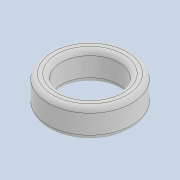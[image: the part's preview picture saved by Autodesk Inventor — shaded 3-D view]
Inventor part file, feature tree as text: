
AUTODESK INVENTOR PART (.ipt)
format: ipt  version: 2020 (Build 240168000, 168)  size: 139,264 bytes
history: native  units: mm
features: extrude x1, fillet x1, sketch x1
ambient origin geometry x8: Origin, YZ Plane, XZ Plane, XY Plane, X Axis, Y Axis, Z Axis, Center Point
bodies: Solid1 (feature_tree)
feature tree (3):
  extrude  "Extrusion1"  Depth=0.25mm
  fillet  "Fillet1"  Radius=1.5mm
  sketch  "Sketch1"  dims[d0=3.0mm d1=0.7mm d2=1.5mm d3=0.0mm d4=0.25mm]
